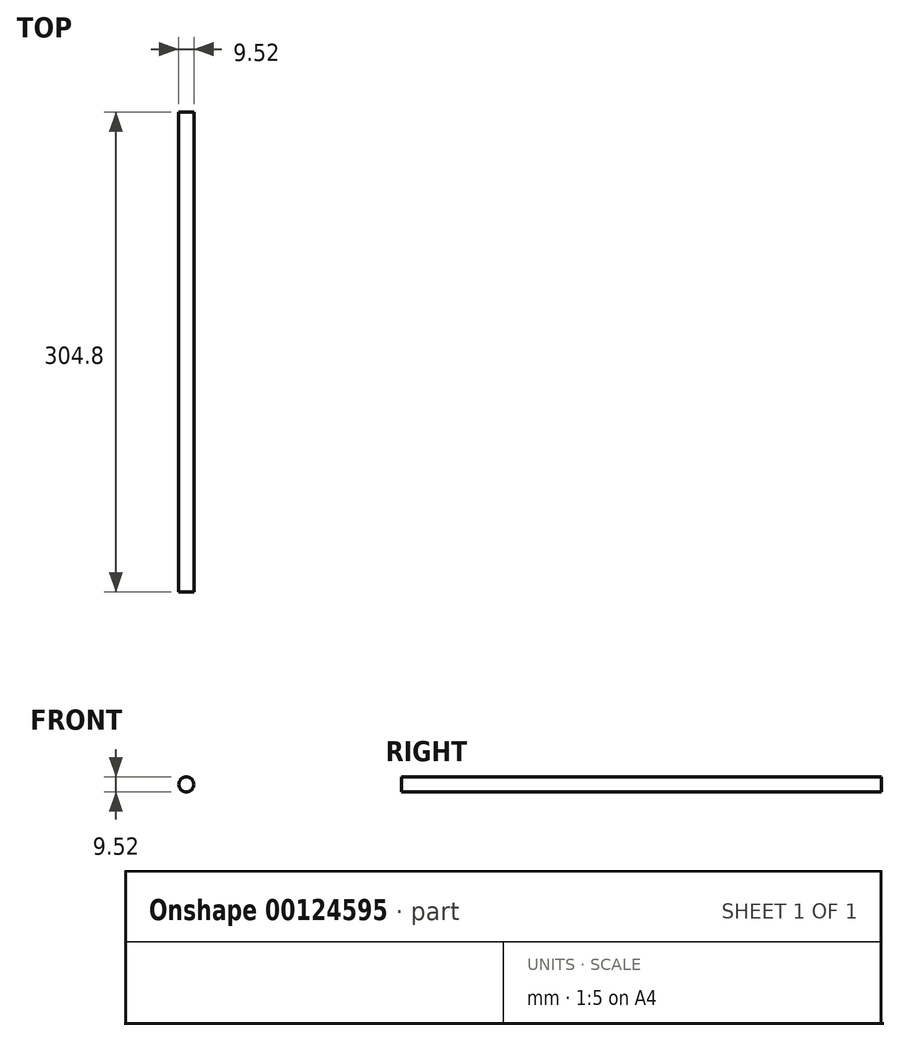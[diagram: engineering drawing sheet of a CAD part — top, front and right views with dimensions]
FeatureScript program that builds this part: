
annotation { "Feature Type Name" : "Feature", "Feature Type Description" : "" }
export const myFeature = defineFeature(function(context is Context, id is Id, definition is map)
    precondition{}
    {
        {
            var Q0;
            Q0=qCreatedBy(makeId("Front.planeOp"),FACE);
            var sketch = newSketch(context, id + "F0", { "sketchPlane" : qUnion([Q0])});
            skCircle(sketch, "E0", {"center": v(0, 0) * mm, "radius": 4.76 * mm});
            skSolve(sketch);
        }
        {
            var Q0;
            Q0 = qSketchRegion(id + "F0", true);
            extrude(context, id + "F1", {"entities" : qUnion([Q0]), "depth" : 304.8 * mm});
        }
    });
